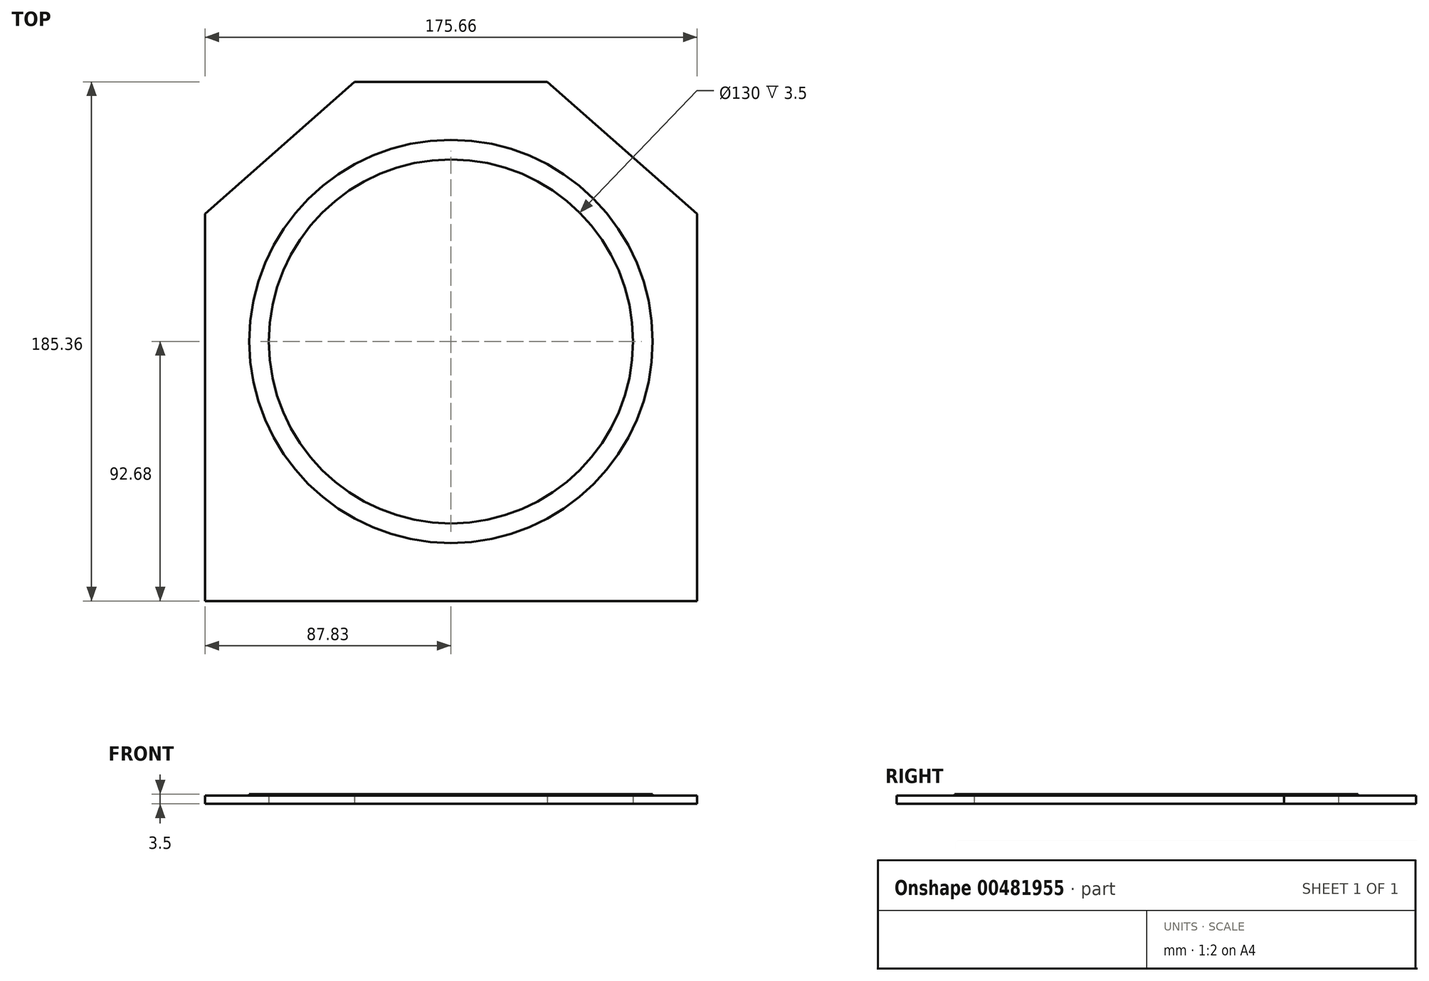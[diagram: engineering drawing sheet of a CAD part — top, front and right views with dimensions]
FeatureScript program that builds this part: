
annotation { "Feature Type Name" : "Feature", "Feature Type Description" : "" }
export const myFeature = defineFeature(function(context is Context, id is Id, definition is map)
    precondition{}
    {
        {
            var Q0;
            Q0=qCreatedBy(makeId("Top.planeOp"),FACE);
            var sketch = newSketch(context, id + "F0", { "sketchPlane" : qUnion([Q0])});
            skLineSegment(sketch, "E0", {"start": v(87.83, -92.68) * mm, "end": v(-87.83, -92.68) * mm});
            skLineSegment(sketch, "E1", {"start": v(-87.83, -92.68) * mm, "end": v(-87.83, 45.57) * mm});
            skLineSegment(sketch, "E2", {"start": v(-87.83, 45.57) * mm, "end": v(-34.43, 92.68) * mm});
            skLineSegment(sketch, "E3", {"start": v(-34.43, 92.68) * mm, "end": v(34.43, 92.68) * mm});
            skLineSegment(sketch, "E4", {"start": v(34.43, 92.68) * mm, "end": v(87.83, 45.57) * mm});
            skLineSegment(sketch, "E5", {"start": v(87.82, 45.57) * mm, "end": v(87.83, -92.68) * mm});
            skCircle(sketch, "E6", {"center": v(0, 0) * mm, "radius": 65 * mm});
            skSolve(sketch);
        }
        {
            var Q0;
            Q0 = qSketchRegion(id + "F0", true);
            extrude(context, id + "F1", {"entities" : qUnion([Q0]), "depth" : 3 * mm});
        }
        {
            var Q0;
            Q0=makeQuery(id+"F1.opExtrude","CAP_FACE",FACE,{"disambiguationData":[OSD([sQuery(id+"F0.wireOp",EDGE,"E0"),sQuery(id+"F0.wireOp",EDGE,"E1"),sQuery(id+"F0.wireOp",EDGE,"E2"),sQuery(id+"F0.wireOp",EDGE,"E3"),sQuery(id+"F0.wireOp",EDGE,"E4"),sQuery(id+"F0.wireOp",EDGE,"E5"),sQuery(id+"F0.wireOp",EDGE,"E6")])],"isStart":false});
            var sketch = newSketch(context, id + "F2", { "sketchPlane" : qUnion([Q0])});
            skCircle(sketch, "E7", {"center": v(0, 0) * mm, "radius": 72 * mm});
            skCircle(sketch, "E8", {"center": v(0, 0) * mm, "radius": 65 * mm});
            skSolve(sketch);
        }
        {
            var Q0;
            Q0 = qSketchRegion(id + "F2", true);
            extrude(context, id + "F3", {"entities" : qUnion([Q0]), "operationType" : NewBodyOperationType.ADD, "depth" : .5 * mm});
        }
    });
